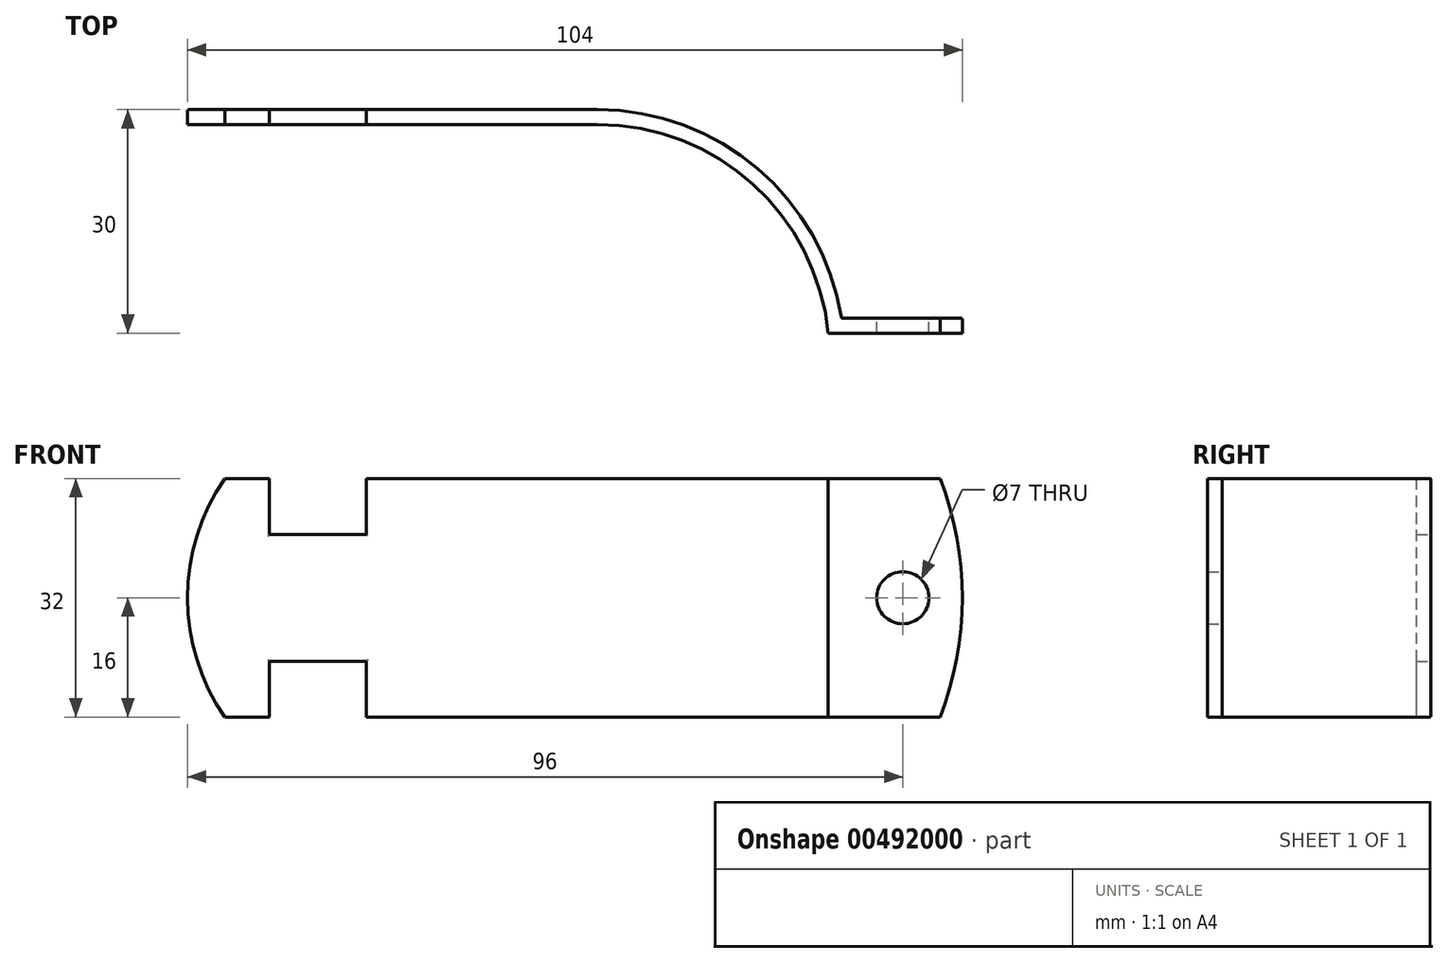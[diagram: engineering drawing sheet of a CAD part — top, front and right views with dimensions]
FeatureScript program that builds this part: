
annotation { "Feature Type Name" : "Feature", "Feature Type Description" : "" }
export const myFeature = defineFeature(function(context is Context, id is Id, definition is map)
    precondition{}
    {
        {
            var Q0;
            Q0=qCreatedBy(makeId("Top.planeOp"),FACE);
            var sketch = newSketch(context, id + "F0", { "sketchPlane" : qUnion([Q0])});
            skLineSegment(sketch, "E0.bottom", {"start": v(27.5, -1) * mm, "end": v(-27.5, -1) * mm});
            skLineSegment(sketch, "E0.top", {"start": v(27.5, 1) * mm, "end": v(-27.5, 1) * mm});
            skLineSegment(sketch, "E0.right", {"start": v(-27.5, -1) * mm, "end": v(-27.5, 1) * mm});
            skPoint(sketch, "E0.middle", {"position": v(0, 0) * mm});
            skLineSegment(sketch, "E1", {"start": v(-27.5, -8.41) * mm, "end": v(58.5, -8.41) * mm, "construction": true});
            skLineSegment(sketch, "E2", {"start": v(27.5, -1) * mm, "end": v(27.5, -29) * mm, "construction": true});
            skLineSegment(sketch, "E3", {"start": v(27.5, -29) * mm, "end": v(58.5, -29) * mm, "construction": true});
            skArc(sketch, "E4", {"start": v(58.5, -29) * mm, "mid": v(48.39, -9.04) * mm, "end": v(27.5, -1) * mm});
            skLineSegment(sketch, "E5", {"start": v(58.5, -29) * mm, "end": v(76.5, -29) * mm});
            skArc(sketch, "E6.0", {"start": v(60.26, -27) * mm, "mid": v(49.05, -6.95) * mm, "end": v(27.5, 1) * mm});
            skLineSegment(sketch, "E7.0", {"start": v(60.26, -27) * mm, "end": v(76.5, -27) * mm});
            skLineSegment(sketch, "E8", {"start": v(76.5, -27) * mm, "end": v(76.5, -29) * mm});
            skSolve(sketch);
        }
        {
            var Q0;
            Q0 = qSketchRegion(id + "F0", true);
            extrude(context, id + "F1", {"entities" : qUnion([Q0]), "endBound" : BoundingType.SYMMETRIC, "depth" : 32 * mm});
        }
        {
            var Q0;
            Q0=makeQuery(id+"F1.opExtrude","SWEPT_FACE",FACE,{"disambiguationData":[OSD([sQuery(id+"F0.wireOp",EDGE,"E5")])]});
            var sketch = newSketch(context, id + "F2", { "sketchPlane" : qUnion([Q0])});
            skLineSegment(sketch, "E9", {"start": v(76.5, 16) * mm, "end": v(73.5, 16) * mm});
            skLineSegment(sketch, "E10", {"start": v(76.5, -16) * mm, "end": v(73.5, -16) * mm});
            skArc(sketch, "E11", {"start": v(73.5, -16) * mm, "mid": v(76.5, 0) * mm, "end": v(73.5, 16) * mm});
            skSolve(sketch);
        }
        {
            var Q0;
            {var subQ0=sQuery(id+"F2.wireOp",EDGE,"E9");Q0=makeQuery(id+"F2.imprint","IMPRINT",FACE,{"disambiguationData":[TD([[makeQuery(id+"F2.imprint","IMPRINT",EDGE,{"derivedFrom":subQ0}),-1.0]])]});}
            var Q1;
            {var subQ0=sQuery(id+"F2.wireOp",EDGE,"E10");Q1=makeQuery(id+"F2.imprint","IMPRINT",FACE,{"disambiguationData":[TD([[makeQuery(id+"F2.imprint","IMPRINT",EDGE,{"derivedFrom":subQ0}),1.0]])]});}
            extrude(context, id + "F3", {"entities" : qUnion([Q0, Q1]), "operationType" : NewBodyOperationType.REMOVE, "endBound" : BoundingType.SYMMETRIC, "oppositeDirection" : true, "depth" : 25 * mm});
        }
        {
            var Q0;
            Q0=makeQuery(id+"F1.opExtrude","SWEPT_FACE",FACE,{"disambiguationData":[OSD([sQuery(id+"F0.wireOp",EDGE,"E0.top")])]});
            var sketch = newSketch(context, id + "F4", { "sketchPlane" : qUnion([Q0])});
            skLineSegment(sketch, "E12.0", {"start": v(27.5, 16) * mm, "end": v(27.5, -16) * mm});
            skLineSegment(sketch, "E13", {"start": v(27.5, -16) * mm, "end": v(22.5, -16) * mm});
            skLineSegment(sketch, "E14", {"start": v(27.5, 16) * mm, "end": v(22.5, 16) * mm});
            skArc(sketch, "E15", {"start": v(22.5, -16) * mm, "mid": v(27.5, 0) * mm, "end": v(22.5, 16) * mm});
            skSolve(sketch);
        }
        {
            var Q0;
            Q0 = qSketchRegion(id + "F4", true);
            extrude(context, id + "F5", {"entities" : qUnion([Q0]), "operationType" : NewBodyOperationType.REMOVE, "endBound" : BoundingType.SYMMETRIC, "depth" : 25 * mm});
        }
        {
            var Q0;
            Q0=makeQuery(id+"F1.opExtrude","SWEPT_FACE",FACE,{"disambiguationData":[OSD([sQuery(id+"F0.wireOp",EDGE,"E0.top")])]});
            var sketch = newSketch(context, id + "F6", { "sketchPlane" : qUnion([Q0])});
            skLineSegment(sketch, "E16", {"start": v(27.5, 0) * mm, "end": v(10, 0) * mm, "construction": true});
            skPoint(sketch, "E16.endSnap0", {"position": v(27.5, 0) * mm});
            skLineSegment(sketch, "E17.bottom", {"start": v(3.5, -8.5) * mm, "end": v(16.5, -8.5) * mm});
            skLineSegment(sketch, "E17.top", {"start": v(3.5, 8.5) * mm, "end": v(16.5, 8.5) * mm});
            skPoint(sketch, "E17.middle", {"position": v(10, 0) * mm});
            skLineSegment(sketch, "E18", {"start": v(16.5, -16) * mm, "end": v(16.5, -8.5) * mm});
            skLineSegment(sketch, "E19", {"start": v(3.5, -16) * mm, "end": v(3.5, -8.5) * mm});
            skLineSegment(sketch, "E20.0", {"start": v(3.5, -16) * mm, "end": v(16.5, -16) * mm});
            skPoint(sketch, "E21.orphan", {"position": v(22.5, -16) * mm});
            skPoint(sketch, "E22.orphan", {"position": v(16.5, -13.95) * mm});
            skPoint(sketch, "E23.orphan", {"position": v(3.5, -14.88) * mm});
            skPoint(sketch, "E24.orphan", {"position": v(-27.5, -16) * mm});
            skLineSegment(sketch, "E25.trimOffspring", {"start": v(3.5, 8.5) * mm, "end": v(3.5, 16) * mm});
            skLineSegment(sketch, "E26.trimOffspring", {"start": v(16.5, 8.5) * mm, "end": v(16.5, 16) * mm});
            skLineSegment(sketch, "E27.0", {"start": v(3.5, 16) * mm, "end": v(16.5, 16) * mm});
            skPoint(sketch, "E28.orphan", {"position": v(22.5, 16) * mm});
            skPoint(sketch, "E29.orphan", {"position": v(-27.5, 16) * mm});
            skSolve(sketch);
        }
        {
            var Q0;
            Q0 = qSketchRegion(id + "F6", true);
            extrude(context, id + "F7", {"entities" : qUnion([Q0]), "operationType" : NewBodyOperationType.REMOVE, "endBound" : BoundingType.SYMMETRIC, "oppositeDirection" : true, "depth" : 25 * mm});
        }
        {
            var Q0;
            Q0=makeQuery(id+"F1.opExtrude","SWEPT_FACE",FACE,{"disambiguationData":[OSD([sQuery(id+"F0.wireOp",EDGE,"E7.0")])]});
            var sketch = newSketch(context, id + "F8", { "sketchPlane" : qUnion([Q0])});
            skLineSegment(sketch, "E30", {"start": v(-68.5, 16) * mm, "end": v(-68.5, -16) * mm, "construction": true});
            skLineSegment(sketch, "E31.0", {"start": v(-60.26, 16) * mm, "end": v(-73.5, 16) * mm, "construction": true});
            skLineSegment(sketch, "E32.0", {"start": v(-60.26, -16) * mm, "end": v(-73.5, -16) * mm, "construction": true});
            skCircle(sketch, "E33", {"center": v(-68.5, 0) * mm, "radius": 3.5 * mm});
            skSolve(sketch);
        }
        {
            var Q0;
            Q0 = qSketchRegion(id + "F8", true);
            extrude(context, id + "F9", {"entities" : qUnion([Q0]), "operationType" : NewBodyOperationType.REMOVE, "endBound" : BoundingType.SYMMETRIC, "oppositeDirection" : true, "depth" : 25 * mm});
        }
        {
            var Q0;
            Q0=makeQuery(id+"F1.opExtrude","SWEPT_FACE",FACE,{"disambiguationData":[OSD([sQuery(id+"F0.wireOp",EDGE,"E7.0")])]});
            var Q1;
            Q1=makeQuery(id+"F1.opExtrude","SWEPT_FACE",FACE,{"disambiguationData":[OSD([sQuery(id+"F0.wireOp",EDGE,"E6.0")])]});
            var Q2;
            Q2=makeQuery(id+"F1.opExtrude","SWEPT_FACE",FACE,{"disambiguationData":[OSD([sQuery(id+"F0.wireOp",EDGE,"E0.top")])]});
            fillet(context, id + "F10", {"entities" : qUnion([Q0, Q1, Q2]), "radius" : .2 * mm, "tangentPropagation" : true, "allowEdgeOverflow" : false});
        }
    });
